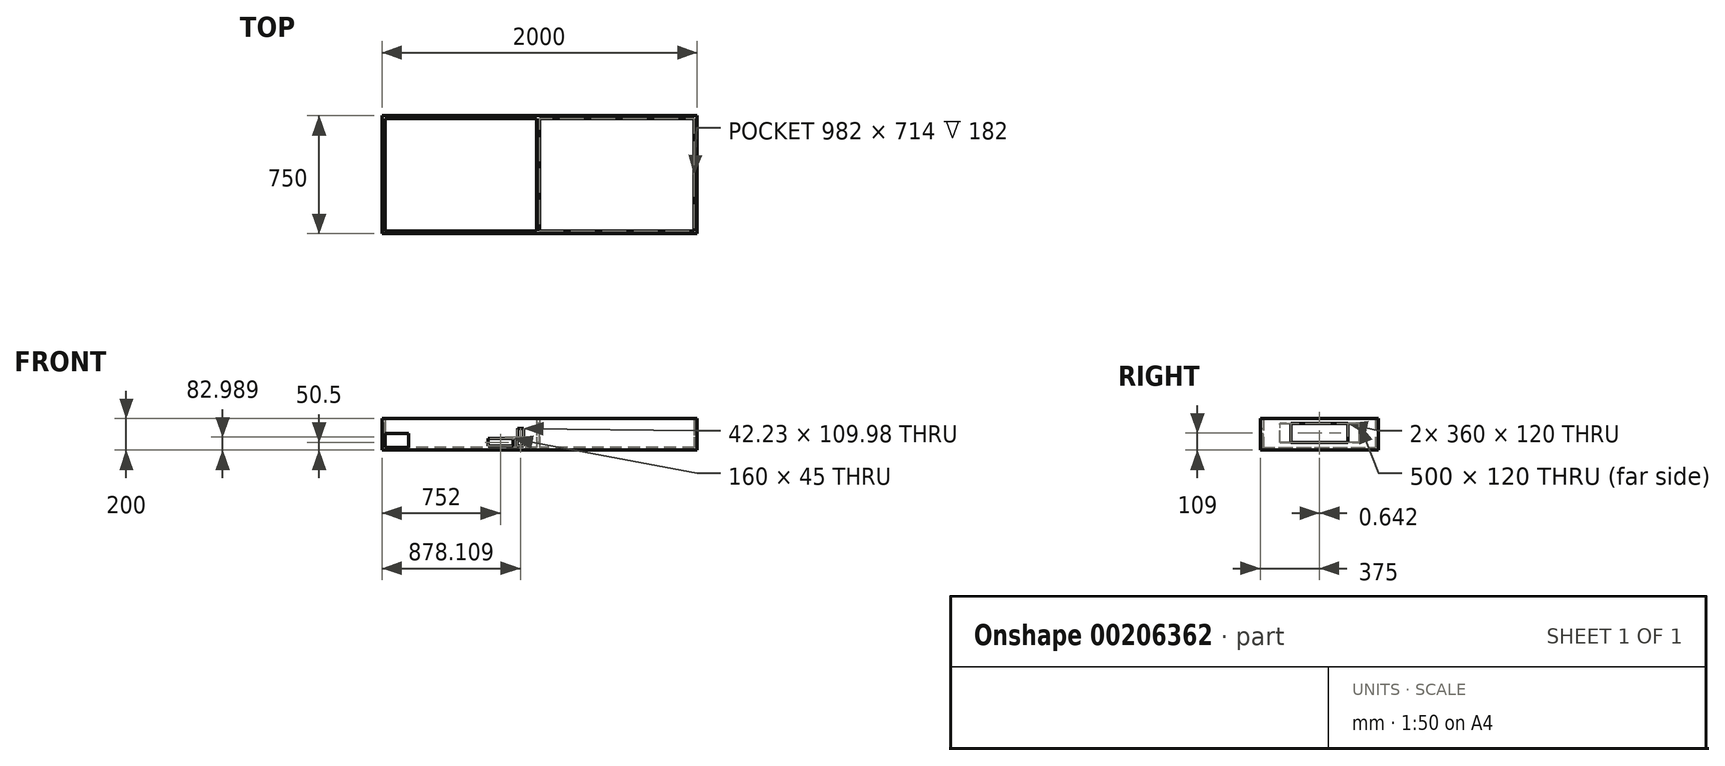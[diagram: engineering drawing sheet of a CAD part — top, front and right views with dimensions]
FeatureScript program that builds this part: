
annotation { "Feature Type Name" : "Feature", "Feature Type Description" : "" }
export const myFeature = defineFeature(function(context is Context, id is Id, definition is map)
    precondition{}
    {
        {
            var Q0;
            Q0=qCreatedBy(makeId("Top.planeOp"),FACE);
            var sketch = newSketch(context, id + "F0", { "sketchPlane" : qUnion([Q0])});
            skLineSegment(sketch, "E0.bottom", {"start": v(1000, -375) * mm, "end": v(-1000, -375) * mm});
            skLineSegment(sketch, "E0.top", {"start": v(1000, 375) * mm, "end": v(-1000, 375) * mm});
            skLineSegment(sketch, "E0.left", {"start": v(1000, -375) * mm, "end": v(1000, 375) * mm});
            skLineSegment(sketch, "E0.right", {"start": v(-1000, -375) * mm, "end": v(-1000, 375) * mm});
            skPoint(sketch, "E0.middle", {"position": v(0, 0) * mm});
            skSolve(sketch);
        }
        {
            var Q0;
            Q0=makeQuery(id+"F0.imprint","IMPRINT",FACE,{"disambiguationData":[TD([[makeQuery(id+"F0.imprint","IMPRINT",EDGE,{"derivedFrom":sQuery(id+"F0.wireOp",EDGE,"E0.bottom")}),-1.0]])]});
            extrude(context, id + "F1", {"entities" : qUnion([Q0]), "depth" : 200 * mm});
        }
        {
            var Q0;
            Q0=makeQuery(id+"F1.opExtrude","CAP_FACE",FACE,{"disambiguationData":[OSD([sQuery(id+"F0.wireOp",EDGE,"E0.bottom"),sQuery(id+"F0.wireOp",EDGE,"E0.top"),sQuery(id+"F0.wireOp",EDGE,"E0.left"),sQuery(id+"F0.wireOp",EDGE,"E0.right")])],"isStart":false});
            shell(context, id + "F2", {"entities" : qUnion([Q0]), "thickness" : 18 * mm});
        }
        {
            var Q0;
            Q0=makeQuery(id+"F2.opShell","OFFSET_FACE",FACE,{"disambiguationData":[OSD([sQuery(id+"F0.wireOp",EDGE,"E0.bottom"),sQuery(id+"F0.wireOp",EDGE,"E0.top"),sQuery(id+"F0.wireOp",EDGE,"E0.left"),sQuery(id+"F0.wireOp",EDGE,"E0.right")])]});
            var sketch = newSketch(context, id + "F3", { "sketchPlane" : qUnion([Q0])});
            skLineSegment(sketch, "E1.bottom", {"start": v(0, 357) * mm, "end": v(-18, 357) * mm});
            skLineSegment(sketch, "E1.top", {"start": v(0, -357) * mm, "end": v(-18, -357) * mm});
            skLineSegment(sketch, "E1.left", {"start": v(0, 357) * mm, "end": v(0, -357) * mm});
            skLineSegment(sketch, "E1.right", {"start": v(-18, 357) * mm, "end": v(-18, -357) * mm});
            skSolve(sketch);
        }
        {
            var Q0;
            Q0=makeQuery(id+"F3.imprint","IMPRINT",FACE,{"disambiguationData":[TD([[makeQuery(id+"F3.imprint","IMPRINT",EDGE,{"derivedFrom":sQuery(id+"F3.wireOp",EDGE,"E1.bottom")}),1.0]])]});
            extrude(context, id + "F4", {"entities" : qUnion([Q0]), "operationType" : NewBodyOperationType.ADD, "depth" : 182 * mm});
        }
        {
            var Q0;
            Q0=makeQuery(id+"F4.opExtrude","SWEPT_FACE",FACE,{"disambiguationData":[OSD([sQuery(id+"F3.wireOp",EDGE,"E1.right")])]});
            var sketch = newSketch(context, id + "F5", { "sketchPlane" : qUnion([Q0])});
            skLineSegment(sketch, "E2", {"start": v(0, 200) * mm, "end": v(0, 169) * mm});
            skLineSegment(sketch, "E3", {"start": v(0, 169) * mm, "end": v(250, 169) * mm});
            skLineSegment(sketch, "E4", {"start": v(250, 169) * mm, "end": v(250, 49) * mm});
            skLineSegment(sketch, "E5", {"start": v(250, 49) * mm, "end": v(-250, 49) * mm});
            skLineSegment(sketch, "E6", {"start": v(-250, 49) * mm, "end": v(-250, 169) * mm});
            skLineSegment(sketch, "E7", {"start": v(-250, 169) * mm, "end": v(0, 169) * mm});
            skSolve(sketch);
        }
        {
            var Q0;
            Q0=makeQuery(id+"F5.imprint","IMPRINT",FACE,{"disambiguationData":[TD([[makeQuery(id+"F5.imprint","IMPRINT",EDGE,{"derivedFrom":sQuery(id+"F5.wireOp",EDGE,"E3")}),-1.0]])]});
            extrude(context, id + "F6", {"entities" : qUnion([Q0]), "operationType" : NewBodyOperationType.REMOVE, "oppositeDirection" : true, "depth" : 25 * mm});
        }
        {
            var Q0;
            {var subQ1=sQuery(id+"F0.wireOp",EDGE,"E0.right");var subQ4=sQuery(id+"F0.wireOp",EDGE,"E0.bottom");Q0=makeQuery(id+"F4.boolean.opBoolean","SPLIT",FACE,{"disambiguationData":[TD([makeQuery(id+"F2.opShell","OFFSET_FACE",FACE,{"disambiguationData":[OSD([subQ1])]})])],"derivedFrom":makeQuery(id+"F2.opShell","OFFSET_FACE",FACE,{"disambiguationData":[OSD([subQ4])]})});}
            var sketch = newSketch(context, id + "F7", { "sketchPlane" : qUnion([Q0])});
            skLineSegment(sketch, "E8.bottom", {"start": v(982, 18) * mm, "end": v(832, 18) * mm});
            skLineSegment(sketch, "E8.top", {"start": v(982, 106.6) * mm, "end": v(832, 106.6) * mm});
            skLineSegment(sketch, "E8.left", {"start": v(982, 18) * mm, "end": v(982, 106.6) * mm});
            skLineSegment(sketch, "E8.right", {"start": v(832, 18) * mm, "end": v(832, 106.6) * mm});
            skLineSegment(sketch, "E9", {"start": v(18, 18) * mm, "end": v(93.34, 18) * mm});
            skLineSegment(sketch, "E10", {"start": v(328, 18) * mm, "end": v(328, 28) * mm});
            skLineSegment(sketch, "E11", {"start": v(328, 28) * mm, "end": v(168, 28) * mm});
            skLineSegment(sketch, "E12", {"start": v(168, 28) * mm, "end": v(168, 18) * mm});
            skLineSegment(sketch, "E13", {"start": v(168, 28) * mm, "end": v(143, 28) * mm});
            skLineSegment(sketch, "E14", {"start": v(143, 28) * mm, "end": v(103, 28) * mm});
            skLineSegment(sketch, "E15", {"start": v(103, 28) * mm, "end": v(18, 28) * mm});
            skLineSegment(sketch, "E16", {"start": v(103, 28) * mm, "end": v(100.78, 137.98) * mm});
            skLineSegment(sketch, "E17", {"start": v(100.78, 137.98) * mm, "end": v(140.78, 137.98) * mm});
            skLineSegment(sketch, "E18", {"start": v(140.78, 137.98) * mm, "end": v(143, 28) * mm});
            skLineSegment(sketch, "E19", {"start": v(168, 28) * mm, "end": v(168, 73) * mm});
            skLineSegment(sketch, "E20", {"start": v(168, 73) * mm, "end": v(328, 73) * mm});
            skLineSegment(sketch, "E21", {"start": v(328, 73) * mm, "end": v(328, 28) * mm});
            skSolve(sketch);
        }
        {
            var Q0;
            Q0=qSketchRegion(id+"F7",true);
            extrude(context, id + "F8", {"entities" : qUnion([Q0]), "operationType" : NewBodyOperationType.REMOVE, "oppositeDirection" : true, "depth" : 25 * mm});
        }
        {
            var Q0;
            Q0=qSketchRegion(id+"F7",true);
            extrude(context, id + "F9", {"entities" : qUnion([Q0]), "operationType" : NewBodyOperationType.REMOVE, "oppositeDirection" : true, "depth" : 25 * mm});
        }
        {
            var Q0;
            Q0=qSketchRegion(id+"F7",true);
            extrude(context, id + "F10", {"entities" : qUnion([Q0]), "operationType" : NewBodyOperationType.REMOVE, "oppositeDirection" : true, "depth" : 25 * mm});
        }
        {
            var Q0;
            Q0=makeQuery(id+"F2.opShell","OFFSET_FACE",FACE,{"disambiguationData":[OSD([sQuery(id+"F0.wireOp",EDGE,"E0.left")])]});
            var sketch = newSketch(context, id + "F11", { "sketchPlane" : qUnion([Q0])});
            skLineSegment(sketch, "E22", {"start": v(-357, 18) * mm, "end": v(0, 18) * mm});
            skLineSegment(sketch, "E23", {"start": v(0, 18) * mm, "end": v(180, 18) * mm});
            skLineSegment(sketch, "E24", {"start": v(180, 18) * mm, "end": v(180, 49) * mm});
            skLineSegment(sketch, "E25", {"start": v(180, 49) * mm, "end": v(180, 169) * mm});
            skLineSegment(sketch, "E26", {"start": v(180, 169) * mm, "end": v(-180, 169) * mm});
            skLineSegment(sketch, "E27", {"start": v(-180, 169) * mm, "end": v(-180, 49) * mm});
            skLineSegment(sketch, "E28", {"start": v(-180, 49) * mm, "end": v(180, 49) * mm});
            skSolve(sketch);
        }
        {
            var Q0;
            Q0=makeQuery(id+"F11.imprint","IMPRINT",FACE,{"disambiguationData":[TD([[makeQuery(id+"F11.imprint","IMPRINT",EDGE,{"derivedFrom":sQuery(id+"F11.wireOp",EDGE,"E25")}),1.0]])]});
            extrude(context, id + "F12", {"entities" : qUnion([Q0]), "operationType" : NewBodyOperationType.ADD, "depth" : 25 * mm});
        }
        {
            var Q0;
            Q0=makeQuery(id+"F12.opExtrude","CAP_FACE",FACE,{"disambiguationData":[OSD([sQuery(id+"F11.wireOp",EDGE,"E25"),sQuery(id+"F11.wireOp",EDGE,"E26"),sQuery(id+"F11.wireOp",EDGE,"E27"),sQuery(id+"F11.wireOp",EDGE,"E28")])],"isStart":false});
            extrude(context, id + "F13", {"entities" : qUnion([Q0]), "operationType" : NewBodyOperationType.REMOVE, "oppositeDirection" : true, "depth" : 25 * mm});
        }
        {
            var Q0;
            Q0=makeQuery(id+"F11.imprint","IMPRINT",FACE,{"disambiguationData":[TD([[makeQuery(id+"F11.imprint","IMPRINT",EDGE,{"derivedFrom":sQuery(id+"F11.wireOp",EDGE,"E25")}),1.0]])]});
            extrude(context, id + "F14", {"entities" : qUnion([Q0]), "operationType" : NewBodyOperationType.REMOVE, "oppositeDirection" : true, "depth" : 25 * mm});
        }
        {
            var Q0;
            Q0=makeQuery(id+"F1.opExtrude","SWEPT_FACE",FACE,{"disambiguationData":[OSD([sQuery(id+"F0.wireOp",EDGE,"E0.right")])]});
            var sketch = newSketch(context, id + "F15", { "sketchPlane" : qUnion([Q0])});
            skLineSegment(sketch, "E29", {"start": v(-180.64, 169.02) * mm, "end": v(179.36, 169.02) * mm});
            skLineSegment(sketch, "E30", {"start": v(179.36, 169.02) * mm, "end": v(179.36, 49.02) * mm});
            skLineSegment(sketch, "E31", {"start": v(179.36, 49.02) * mm, "end": v(-180.64, 49.02) * mm});
            skLineSegment(sketch, "E32", {"start": v(-180.64, 49.02) * mm, "end": v(-180.64, 169.02) * mm});
            skSolve(sketch);
        }
        {
            var Q0;
            Q0=makeQuery(id+"F15.imprint","IMPRINT",FACE,{"disambiguationData":[TD([[makeQuery(id+"F15.imprint","IMPRINT",EDGE,{"derivedFrom":sQuery(id+"F15.wireOp",EDGE,"E29")}),-1.0]])]});
            extrude(context, id + "F16", {"entities" : qUnion([Q0]), "operationType" : NewBodyOperationType.REMOVE, "oppositeDirection" : true, "depth" : 20 * mm});
        }
    });
